# Revit family: PRD_AR_ShwrHds_ShowerHead_SHAS0011
name_source: partatom
category: Plumbing Fixtures
revit_build: Autodesk Revit 2018 (Build: 20190510_1515(x64)
units: mm (PartAtom-declared; Revit-internal decimal feet)

## family parameters
Cut with Voids When Loaded = Yes
Host = Face
OmniClass Number = 23.45.55.14
OmniClass Title = Single Faucets
Part Type = Normal
Room Calculation Point = No
Round Connector Dimension = Use Diameter
Shared = Yes

## types (1)
- SHAS0011
    AdjustableTiltAngle = No
    AssetType = Fixed
    BIMObjectName = PRD_AR_ShwrHds_ShowerHead_SHAS0011
    Category = Pr_40_20_87_76, Shower heads
    Default Elevation = 2100 mm
    Description = AQUAJET-Slimline shower head with plastic jet face with anti-limescale system and low aerosol formation. For installation on KWC shower panels with DN 15 connecting nozzles, diameter 26 mm, high-polished chrome-plated brass.
    DiameterNominal = 15  [stored 0.0492126 ft]
    DrainSize = 0 mm  [stored 0 ft]
    DurationUnit = year
    Features = diameter 26 mm, high-polished chrome-plated brass
    Finish = high-polished
    GrossWeight = 0.60 kg
    HasTray = No
    IfcExportAs = IfcSanitaryTerminalType
    IfcExportType = SHOWER
    InletSize = DN 15
    Manufacturer = KWC Group AG
    ManufacturerName = KWC Group AG
    ManufacturerURL = www.kwc.com
    Material = chrome-plated brass
    MinimumFlowPressure = 1.00 bar
    Model = SHAS0011
    ModelNumber = 2030054255
    ModelReference = SHAS0011
    NBSDescription = Shower heads
    NBSReference = 45-35-70/333
    Name = Shower Head SHAS0011
    NetWeight = 0.50 kg
    NominalDepth = 83 mm  [stored 0.27231 ft]
    NominalHeight = 60 mm  [stored 0.19685 ft]
    NominalWidth = 70 mm  [stored 0.229659 ft]
    ProductInformation = https://pim.kwc.com
    ShowerHeadDescription = Spray shower head
    ShowerHeadMaterial = PRD_AR_ChromatedBrass_HighPolished
    ShowerType = Individual
    Size = 70 x 60 x 83 mm (W x H x D)
    SpoutProjection = 58.00 mm
    TailorMade = No
    Type = Shower head
    TypeOfConnection = Panel
    TypeOfShowerHead = Spray shower head
    URL = www.kwc.com
    Uniclass2015Code = Pr_40_20_87_76
    Uniclass2015Title = Shower heads
    Uniclass2015Version = Products v1.17
    Version = 1
    WarrantyDurationUnit = year

note: [stored X ft] marks values corroborated as IEEE doubles in the binary element streams (Revit-internal decimal feet)

## geometry (parser evidence)
native form markers: Sweep x3
no freeform markers — native parametric forms only
